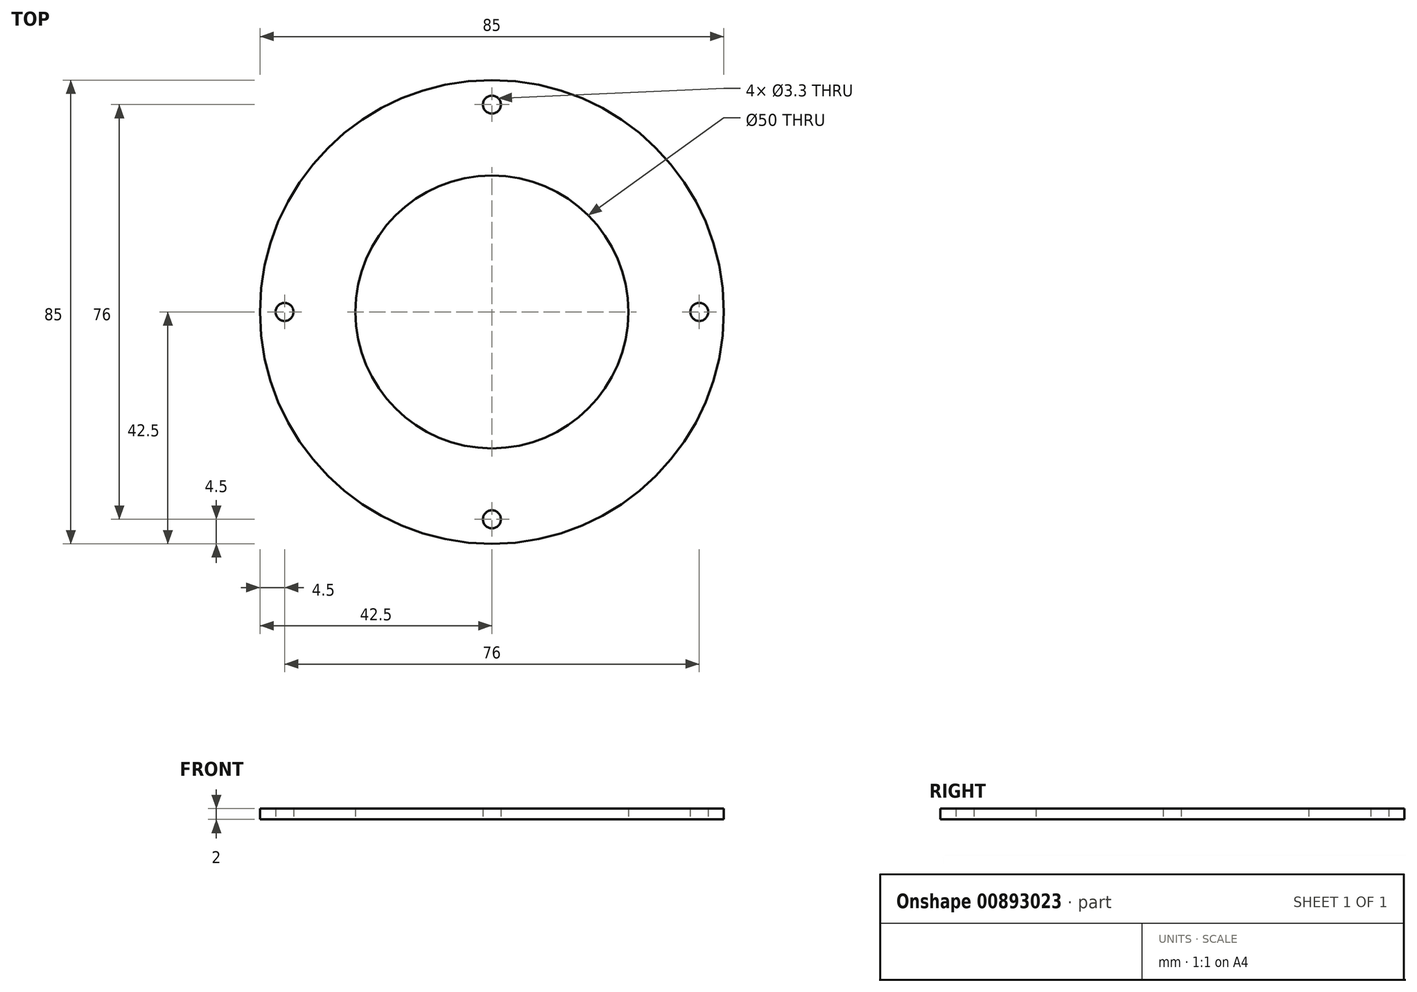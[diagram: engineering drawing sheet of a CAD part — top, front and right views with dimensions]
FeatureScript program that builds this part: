
annotation { "Feature Type Name" : "Feature", "Feature Type Description" : "" }
export const myFeature = defineFeature(function(context is Context, id is Id, definition is map)
    precondition{}
    {
        {
            var Q0;
            Q0=qCreatedBy(makeId("Top.planeOp"),FACE);
            var sketch = newSketch(context, id + "F0", { "sketchPlane" : qUnion([Q0])});
            skCircle(sketch, "E0", {"center": v(0, 0) * mm, "radius": 42.5 * mm});
            skCircle(sketch, "E1", {"center": v(0, 0) * mm, "radius": 25 * mm});
            skLineSegment(sketch, "E2", {"start": v(0, 0) * mm, "end": v(-38, 0) * mm, "construction": true});
            skLineSegment(sketch, "E3", {"start": v(0, 0) * mm, "end": v(0, 38) * mm, "construction": true});
            skCircle(sketch, "E4", {"center": v(-38, 0) * mm, "radius": 1.65 * mm});
            skCircle(sketch, "E5", {"center": v(0, 38) * mm, "radius": 1.65 * mm});
            skCircle(sketch, "E6.MirrorC", {"center": v(0, -38) * mm, "radius": 1.65 * mm});
            skCircle(sketch, "E7.MirrorC", {"center": v(38, 0) * mm, "radius": 1.65 * mm});
            skSolve(sketch);
        }
        {
            var Q0;
            Q0 = qSketchRegion(id + "F0", true);
            extrude(context, id + "F1", {"entities" : qUnion([Q0]), "depth" : 2 * mm, "offsetDistance" : 25 * mm});
        }
    });
